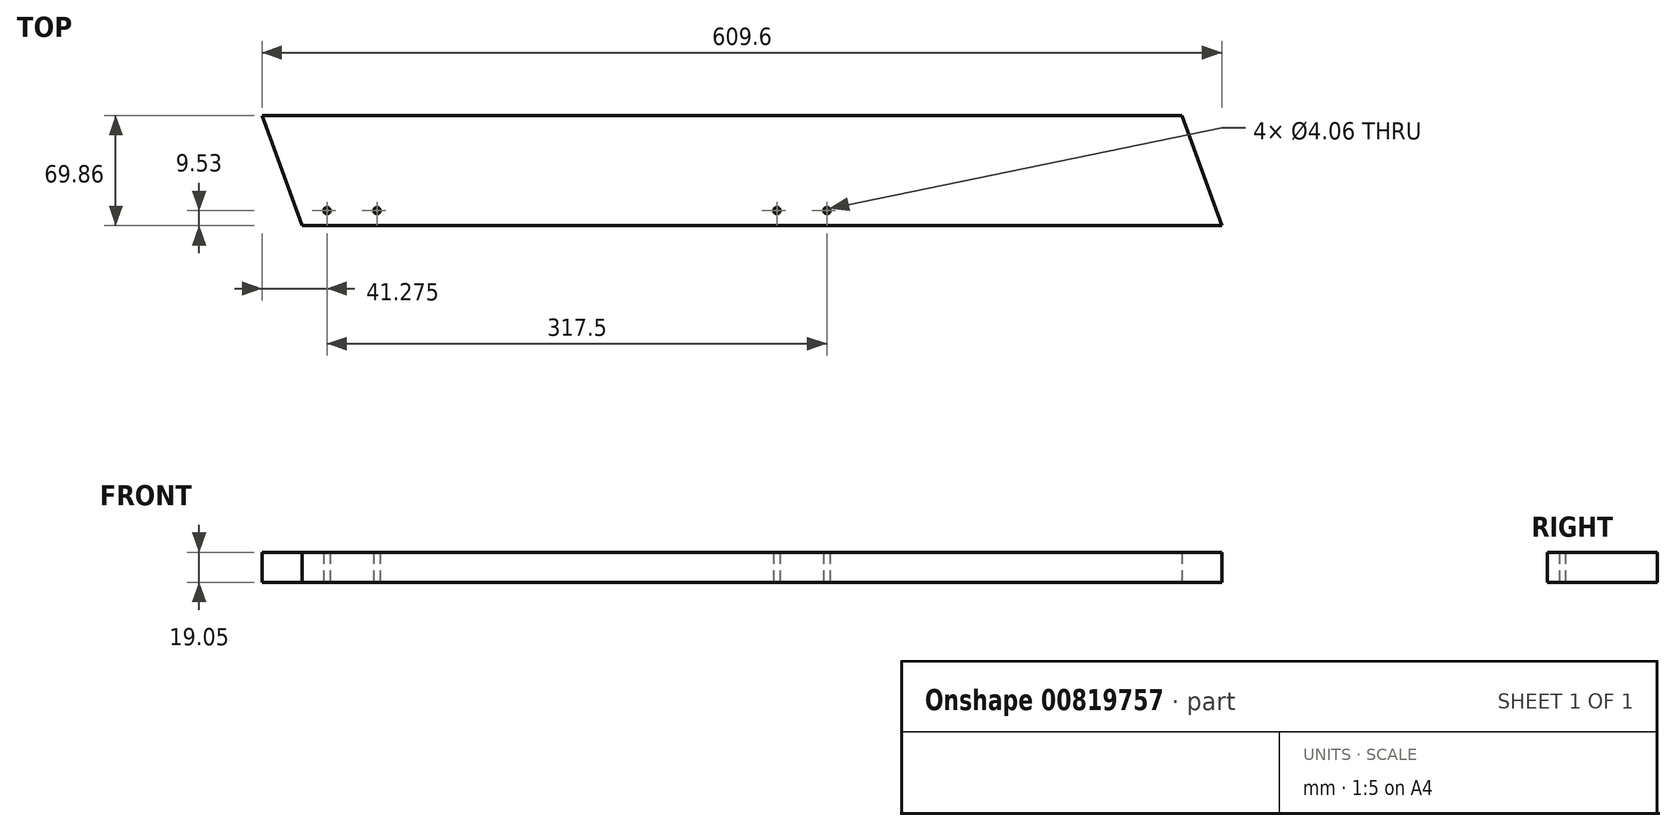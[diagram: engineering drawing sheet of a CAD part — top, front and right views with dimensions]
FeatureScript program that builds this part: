
annotation { "Feature Type Name" : "Feature", "Feature Type Description" : "" }
export const myFeature = defineFeature(function(context is Context, id is Id, definition is map)
    precondition{}
    {
        {
            var Q0;
            Q0=qCreatedBy(makeId("Top.planeOp"),FACE);
            var sketch = newSketch(context, id + "F0", { "sketchPlane" : qUnion([Q0])});
            skLineSegment(sketch, "E0.bottom", {"start": v(-304.8, -34.93) * mm, "end": v(304.8, -34.93) * mm, "construction": true});
            skLineSegment(sketch, "E0.top", {"start": v(-304.8, 34.93) * mm, "end": v(304.8, 34.93) * mm, "construction": true});
            skLineSegment(sketch, "E0.left", {"start": v(-304.8, -34.93) * mm, "end": v(-304.8, 34.93) * mm, "construction": true});
            skLineSegment(sketch, "E0.right", {"start": v(304.8, -34.93) * mm, "end": v(304.8, 34.93) * mm, "construction": true});
            skPoint(sketch, "E0.middle", {"position": v(0, 0) * mm});
            skLineSegment(sketch, "E1", {"start": v(-279.4, 34.93) * mm, "end": v(-279.4, -34.93) * mm, "construction": true});
            skLineSegment(sketch, "E2", {"start": v(279.4, 34.92) * mm, "end": v(279.4, -34.93) * mm, "construction": true});
            skLineSegment(sketch, "E3", {"start": v(-304.8, 34.93) * mm, "end": v(-279.4, -34.93) * mm});
            skLineSegment(sketch, "E4", {"start": v(-279.4, -34.93) * mm, "end": v(304.8, -34.93) * mm});
            skLineSegment(sketch, "E5", {"start": v(304.8, -34.93) * mm, "end": v(279.4, 34.92) * mm});
            skLineSegment(sketch, "E6", {"start": v(279.4, 34.92) * mm, "end": v(-304.8, 34.93) * mm});
            skLineSegment(sketch, "E7", {"start": v(-304.8, -25.4) * mm, "end": v(304.8, -25.4) * mm, "construction": true});
            skLineSegment(sketch, "E8", {"start": v(53.98, 34.92) * mm, "end": v(53.98, -34.93) * mm, "construction": true});
            skLineSegment(sketch, "E9", {"start": v(22.23, 34.92) * mm, "end": v(22.23, -34.93) * mm, "construction": true});
            skLineSegment(sketch, "E10", {"start": v(-231.77, 34.92) * mm, "end": v(-231.77, -34.93) * mm, "construction": true});
            skLineSegment(sketch, "E11", {"start": v(-263.53, 34.92) * mm, "end": v(-263.53, -34.93) * mm, "construction": true});
            skCircle(sketch, "E12", {"center": v(-263.53, -25.4) * mm, "radius": 2.03 * mm});
            skCircle(sketch, "E13", {"center": v(-231.77, -25.4) * mm, "radius": 2.03 * mm});
            skCircle(sketch, "E14", {"center": v(22.23, -25.4) * mm, "radius": 2.03 * mm});
            skCircle(sketch, "E15", {"center": v(53.98, -25.4) * mm, "radius": 2.03 * mm});
            skSolve(sketch);
        }
        {
            var Q0;
            Q0=makeQuery(id+"F0.imprint","IMPRINT",FACE,{"disambiguationData":[TD([[makeQuery(id+"F0.imprint","IMPRINT",EDGE,{"derivedFrom":sQuery(id+"F0.wireOp",EDGE,"E3")}),1.0]])]});
            extrude(context, id + "F1", {"entities" : qUnion([Q0]), "depth" : 19.05 * mm, "offsetDistance" : 25.4 * mm});
        }
    });
